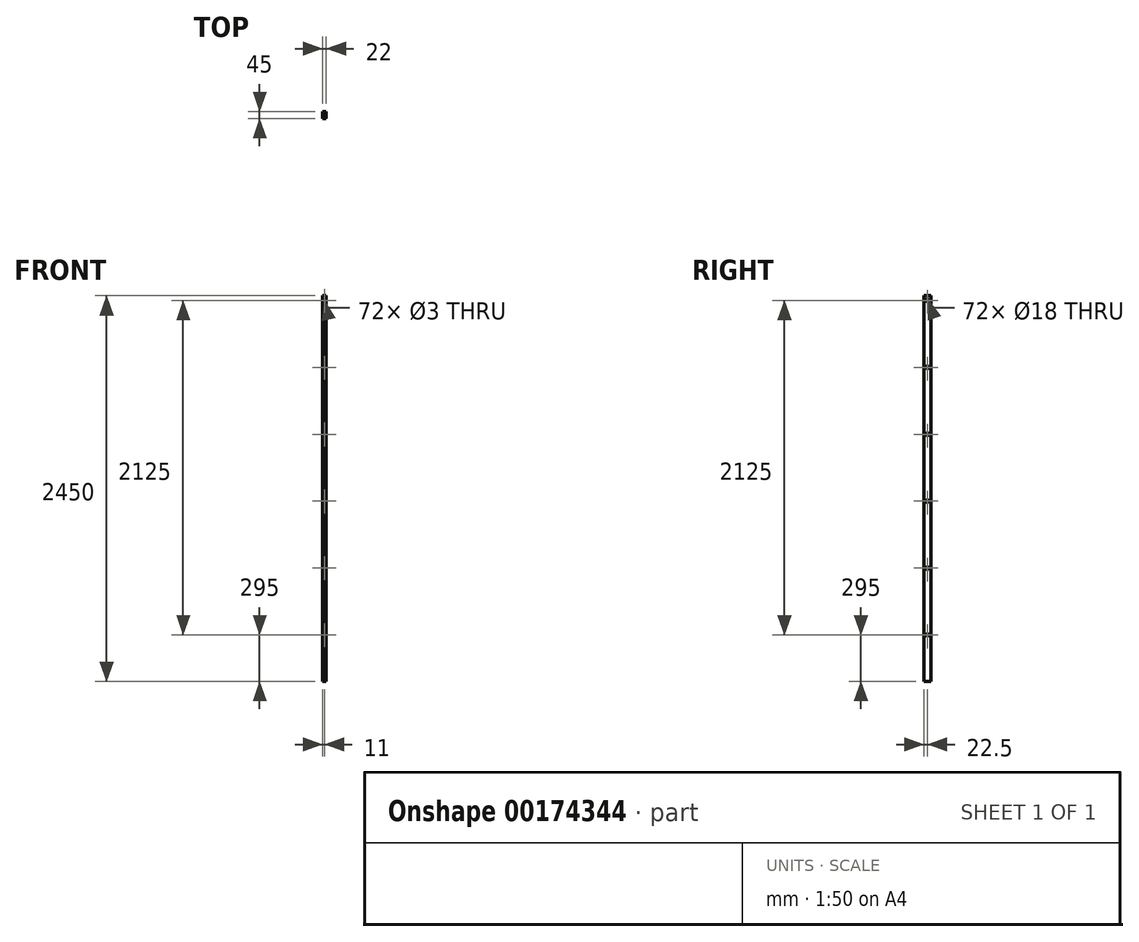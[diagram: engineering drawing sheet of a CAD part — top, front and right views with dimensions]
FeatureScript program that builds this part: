
annotation { "Feature Type Name" : "Feature", "Feature Type Description" : "" }
export const myFeature = defineFeature(function(context is Context, id is Id, definition is map)
    precondition{}
    {
        {
            var Q0;
            Q0=qCreatedBy(makeId("Front.planeOp"),FACE);
            var sketch = newSketch(context, id + "F0", { "sketchPlane" : qUnion([Q0])});
            skLineSegment(sketch, "E0.bottom", {"start": v(-11, 1225) * mm, "end": v(11, 1225) * mm});
            skLineSegment(sketch, "E0.top", {"start": v(-11, -1225) * mm, "end": v(11, -1225) * mm});
            skLineSegment(sketch, "E0.left", {"start": v(-11, 1225) * mm, "end": v(-11, -1225) * mm});
            skLineSegment(sketch, "E0.right", {"start": v(11, 1225) * mm, "end": v(11, -1225) * mm});
            skPoint(sketch, "E0.middle", {"position": v(0, 0) * mm});
            skSolve(sketch);
        }
        {
            var Q0;
            Q0=makeQuery(id+"F0.imprint","IMPRINT",FACE,{"disambiguationData":[TD([[makeQuery(id+"F0.imprint","IMPRINT",EDGE,{"derivedFrom":sQuery(id+"F0.wireOp",EDGE,"E0.bottom")}),-1.0]])]});
            extrude(context, id + "F1", {"entities" : qUnion([Q0]), "depth" : 45 * mm});
        }
        {
            var Q0;
            Q0=makeQuery(id+"F1.opExtrude","CAP_FACE",FACE,{"disambiguationData":[OSD([sQuery(id+"F0.wireOp",EDGE,"E0.bottom"),sQuery(id+"F0.wireOp",EDGE,"E0.top"),sQuery(id+"F0.wireOp",EDGE,"E0.left"),sQuery(id+"F0.wireOp",EDGE,"E0.right")])],"isStart":false});
            var sketch = newSketch(context, id + "F2", { "sketchPlane" : qUnion([Q0])});
            skPoint(sketch, "E1", {"position": v(0, 1195) * mm});
            skPoint(sketch, "E2", {"position": v(0, 770) * mm});
            skPoint(sketch, "E3", {"position": v(0, 345) * mm});
            skPoint(sketch, "E4", {"position": v(0, -80) * mm});
            skPoint(sketch, "E5", {"position": v(0, -505) * mm});
            skPoint(sketch, "E6", {"position": v(0, -930) * mm});
            skSolve(sketch);
        }
        {
            var Q0;
            Q0=sQuery(id+"F2.wireOp",VERTEX,"E1");
            var Q1;
            Q1=sQuery(id+"F2.wireOp",VERTEX,"E2");
            var Q2;
            Q2=sQuery(id+"F2.wireOp",VERTEX,"E5");
            var Q3;
            Q3=sQuery(id+"F2.wireOp",VERTEX,"E3");
            var Q4;
            Q4=sQuery(id+"F2.wireOp",VERTEX,"E6");
            var Q5;
            Q5=sQuery(id+"F2.wireOp",VERTEX,"E4");
            var Q6;
            Q6=makeQuery(id+"F1.opExtrude","SWEPT_BODY",BODY,{"disambiguationData":[OSD([sQuery(id+"F0.wireOp",EDGE,"E0.bottom"),sQuery(id+"F0.wireOp",EDGE,"E0.top"),sQuery(id+"F0.wireOp",EDGE,"E0.left"),sQuery(id+"F0.wireOp",EDGE,"E0.right")])]});
            hole(context, id + "F3", {"style" : HoleStyle.SIMPLE, "endStyle" : HoleEndStyle.BLIND, "holeDiameter" : 3 * mm, "holeDepth" : 22 * mm, "startFromSketch" : true, "locations" : qUnion([Q0, Q1, Q2, Q3, Q4, Q5]), "scope" : qUnion([Q6])});
        }
        {
            var Q0;
            Q0=makeQuery(id+"F1.opExtrude","SWEPT_FACE",FACE,{"disambiguationData":[OSD([sQuery(id+"F0.wireOp",EDGE,"E0.right")])]});
            var sketch = newSketch(context, id + "F4", { "sketchPlane" : qUnion([Q0])});
            skPoint(sketch, "E7", {"position": v(-22.5, 1195) * mm});
            skPoint(sketch, "E7.positionSnap0", {"position": v(-22.5, 1225) * mm});
            skPoint(sketch, "E8", {"position": v(-22.5, 770) * mm});
            skPoint(sketch, "E9", {"position": v(-22.5, 345) * mm});
            skPoint(sketch, "E10", {"position": v(-22.5, -80) * mm});
            skPoint(sketch, "E11", {"position": v(-22.5, -930) * mm});
            skPoint(sketch, "E12", {"position": v(-22.5, -505) * mm});
            skSolve(sketch);
        }
        {
            var Q0;
            Q0=sQuery(id+"F4.wireOp",VERTEX,"E7");
            var Q1;
            Q1=sQuery(id+"F4.wireOp",VERTEX,"E8");
            var Q2;
            Q2=sQuery(id+"F4.wireOp",VERTEX,"E9");
            var Q3;
            Q3=sQuery(id+"F4.wireOp",VERTEX,"E10");
            var Q4;
            Q4=sQuery(id+"F4.wireOp",VERTEX,"E12");
            var Q5;
            Q5=sQuery(id+"F4.wireOp",VERTEX,"E11");
            var Q6;
            Q6=makeQuery(id+"F1.opExtrude","SWEPT_BODY",BODY,{"disambiguationData":[OSD([sQuery(id+"F0.wireOp",EDGE,"E0.bottom"),sQuery(id+"F0.wireOp",EDGE,"E0.top"),sQuery(id+"F0.wireOp",EDGE,"E0.left"),sQuery(id+"F0.wireOp",EDGE,"E0.right")])]});
            hole(context, id + "F5", {"style" : HoleStyle.SIMPLE, "endStyle" : HoleEndStyle.THROUGH, "holeDiameter" : 18 * mm, "startFromSketch" : true, "locations" : qUnion([Q0, Q1, Q2, Q3, Q4, Q5]), "scope" : qUnion([Q6]), "isTappedThrough" : true});
        }
    });
